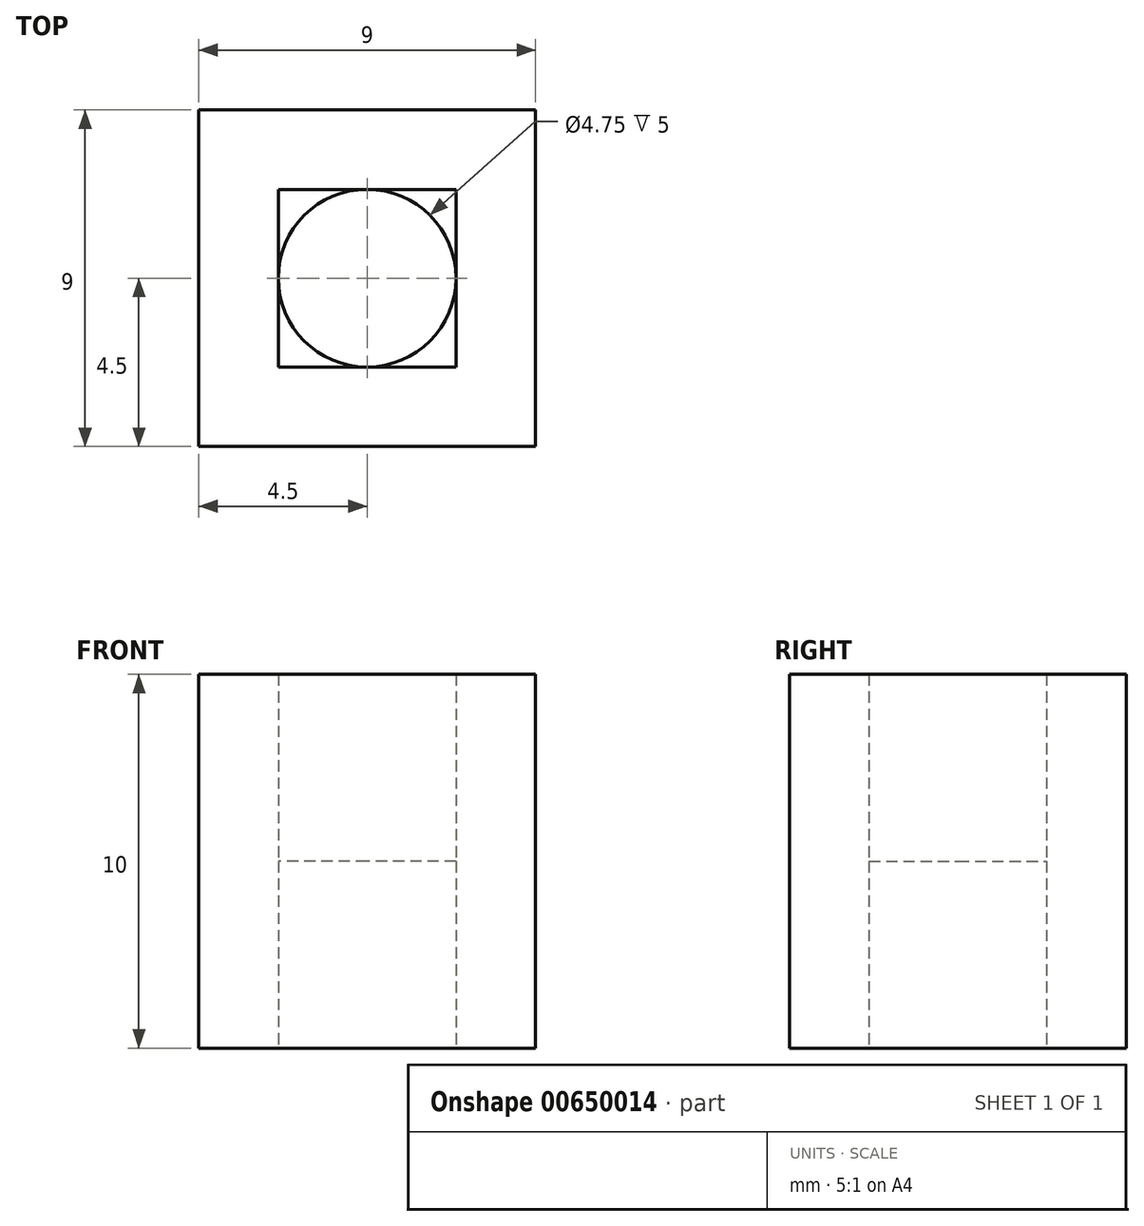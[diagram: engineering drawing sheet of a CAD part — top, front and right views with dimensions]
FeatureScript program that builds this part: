
annotation { "Feature Type Name" : "Feature", "Feature Type Description" : "" }
export const myFeature = defineFeature(function(context is Context, id is Id, definition is map)
    precondition{}
    {
        {
            var Q0;
            Q0=qCreatedBy(makeId("Top.planeOp"),FACE);
            var sketch = newSketch(context, id + "F0", { "sketchPlane" : qUnion([Q0])});
            skCircle(sketch, "E0", {"center": v(0, 0) * mm, "radius": 4.5 * mm});
            skCircle(sketch, "E1", {"center": v(0, 0) * mm, "radius": 2.38 * mm});
            skLineSegment(sketch, "E2.bottom", {"start": v(4.5, -4.5) * mm, "end": v(-4.5, -4.5) * mm});
            skLineSegment(sketch, "E2.top", {"start": v(4.5, 4.5) * mm, "end": v(-4.5, 4.5) * mm});
            skLineSegment(sketch, "E2.left", {"start": v(4.5, -4.5) * mm, "end": v(4.5, 4.5) * mm});
            skLineSegment(sketch, "E2.right", {"start": v(-4.5, -4.5) * mm, "end": v(-4.5, 4.5) * mm});
            skLineSegment(sketch, "E3.bottom", {"start": v(2.38, -2.38) * mm, "end": v(-2.38, -2.38) * mm});
            skLineSegment(sketch, "E3.top", {"start": v(2.38, 2.38) * mm, "end": v(-2.38, 2.38) * mm});
            skLineSegment(sketch, "E3.left", {"start": v(2.38, -2.38) * mm, "end": v(2.38, 2.38) * mm});
            skLineSegment(sketch, "E3.right", {"start": v(-2.38, -2.38) * mm, "end": v(-2.38, 2.38) * mm});
            skSolve(sketch);
        }
        {
            var Q0;
            Q0=makeQuery(id+"F0.imprint","IMPRINT",FACE,{"disambiguationData":[TD([[makeQuery(id+"F0.imprint","IMPRINT",EDGE,{"derivedFrom":sQuery(id+"F0.wireOp",EDGE,"E0")}),1.0]])]});
            var Q1;
            {var subQ0=sQuery(id+"F0.wireOp",EDGE,"E2.top");var subQ1=sQuery(id+"F0.wireOp",EDGE,"E0");var subQ2=makeQuery(id+"F0.imprint","INTERSECT",VERTEX,{"derivedFrom":[subQ1,subQ0]});Q1=makeQuery(id+"F0.imprint","IMPRINT",FACE,{"disambiguationData":[TD([[makeQuery(id+"F0.imprint","IMPRINT",EDGE,{"disambiguationData":[TD([[subQ2,-1.0]])],"derivedFrom":subQ1}),-1.0]])]});}
            var Q2;
            {var subQ0=sQuery(id+"F0.wireOp",EDGE,"E2.top");var subQ1=sQuery(id+"F0.wireOp",EDGE,"E0");var subQ2=makeQuery(id+"F0.imprint","INTERSECT",VERTEX,{"derivedFrom":[subQ1,subQ0]});Q2=makeQuery(id+"F0.imprint","IMPRINT",FACE,{"disambiguationData":[TD([[makeQuery(id+"F0.imprint","IMPRINT",EDGE,{"disambiguationData":[TD([[subQ2,1.0]])],"derivedFrom":subQ1}),-1.0]])]});}
            var Q3;
            {var subQ0=sQuery(id+"F0.wireOp",EDGE,"E2.left");var subQ1=sQuery(id+"F0.wireOp",EDGE,"E0");var subQ2=makeQuery(id+"F0.imprint","INTERSECT",VERTEX,{"derivedFrom":[subQ1,subQ0]});Q3=makeQuery(id+"F0.imprint","IMPRINT",FACE,{"disambiguationData":[TD([[makeQuery(id+"F0.imprint","IMPRINT",EDGE,{"disambiguationData":[TD([[subQ2,1.0]])],"derivedFrom":subQ1}),-1.0]])]});}
            var Q4;
            {var subQ0=sQuery(id+"F0.wireOp",EDGE,"E2.right");var subQ1=sQuery(id+"F0.wireOp",EDGE,"E0");var subQ2=makeQuery(id+"F0.imprint","INTERSECT",VERTEX,{"derivedFrom":[subQ1,subQ0]});Q4=makeQuery(id+"F0.imprint","IMPRINT",FACE,{"disambiguationData":[TD([[makeQuery(id+"F0.imprint","IMPRINT",EDGE,{"disambiguationData":[TD([[subQ2,-1.0]])],"derivedFrom":subQ1}),-1.0]])]});}
            var Q5;
            {var subQ0=sQuery(id+"F0.wireOp",EDGE,"E3.top");var subQ1=sQuery(id+"F0.wireOp",EDGE,"E1");var subQ2=makeQuery(id+"F0.imprint","INTERSECT",VERTEX,{"derivedFrom":[subQ1,subQ0]});Q5=makeQuery(id+"F0.imprint","IMPRINT",FACE,{"disambiguationData":[TD([[makeQuery(id+"F0.imprint","IMPRINT",EDGE,{"disambiguationData":[TD([[subQ2,-1.0]])],"derivedFrom":subQ1}),-1.0]])]});}
            var Q6;
            {var subQ0=sQuery(id+"F0.wireOp",EDGE,"E3.right");var subQ1=sQuery(id+"F0.wireOp",EDGE,"E1");var subQ2=makeQuery(id+"F0.imprint","INTERSECT",VERTEX,{"derivedFrom":[subQ1,subQ0]});Q6=makeQuery(id+"F0.imprint","IMPRINT",FACE,{"disambiguationData":[TD([[makeQuery(id+"F0.imprint","IMPRINT",EDGE,{"disambiguationData":[TD([[subQ2,-1.0]])],"derivedFrom":subQ1}),-1.0]])]});}
            var Q7;
            {var subQ0=sQuery(id+"F0.wireOp",EDGE,"E3.left");var subQ1=sQuery(id+"F0.wireOp",EDGE,"E1");var subQ2=makeQuery(id+"F0.imprint","INTERSECT",VERTEX,{"derivedFrom":[subQ1,subQ0]});Q7=makeQuery(id+"F0.imprint","IMPRINT",FACE,{"disambiguationData":[TD([[makeQuery(id+"F0.imprint","IMPRINT",EDGE,{"disambiguationData":[TD([[subQ2,1.0]])],"derivedFrom":subQ1}),-1.0]])]});}
            var Q8;
            {var subQ0=sQuery(id+"F0.wireOp",EDGE,"E3.top");var subQ1=sQuery(id+"F0.wireOp",EDGE,"E1");var subQ2=makeQuery(id+"F0.imprint","INTERSECT",VERTEX,{"derivedFrom":[subQ1,subQ0]});Q8=makeQuery(id+"F0.imprint","IMPRINT",FACE,{"disambiguationData":[TD([[makeQuery(id+"F0.imprint","IMPRINT",EDGE,{"disambiguationData":[TD([[subQ2,1.0]])],"derivedFrom":subQ1}),-1.0]])]});}
            extrude(context, id + "F1", {"entities" : qUnion([Q0, Q1, Q2, Q3, Q4, Q5, Q6, Q7, Q8]), "depth" : 5 * mm, "offsetDistance" : 25 * mm});
        }
        {
            var Q0;
            {var subQ0=sQuery(id+"F0.wireOp",EDGE,"E2.top");var subQ1=sQuery(id+"F0.wireOp",EDGE,"E0");var subQ2=makeQuery(id+"F0.imprint","INTERSECT",VERTEX,{"derivedFrom":[subQ1,subQ0]});Q0=makeQuery(id+"F0.imprint","IMPRINT",FACE,{"disambiguationData":[TD([[makeQuery(id+"F0.imprint","IMPRINT",EDGE,{"disambiguationData":[TD([[subQ2,-1.0]])],"derivedFrom":subQ1}),-1.0]])]});}
            var Q1;
            {var subQ12=sQuery(id+"F0.wireOp",EDGE,"E0");var subQ13=makeQuery(id+"F0.imprint","INTERSECT",VERTEX,{"derivedFrom":[subQ12,sQuery(id+"F0.wireOp",EDGE,"E2.top")]});Q1=makeQuery(id+"F0.imprint","IMPRINT",FACE,{"disambiguationData":[TD([[makeQuery(id+"F0.imprint","IMPRINT",EDGE,{"disambiguationData":[TD([[subQ13,1.0]])],"derivedFrom":subQ12}),1.0]])]});}
            var Q2;
            {var subQ0=sQuery(id+"F0.wireOp",EDGE,"E2.right");var subQ1=sQuery(id+"F0.wireOp",EDGE,"E0");var subQ2=makeQuery(id+"F0.imprint","INTERSECT",VERTEX,{"derivedFrom":[subQ1,subQ0]});Q2=makeQuery(id+"F0.imprint","IMPRINT",FACE,{"disambiguationData":[TD([[makeQuery(id+"F0.imprint","IMPRINT",EDGE,{"disambiguationData":[TD([[subQ2,-1.0]])],"derivedFrom":subQ1}),-1.0]])]});}
            var Q3;
            {var subQ0=sQuery(id+"F0.wireOp",EDGE,"E2.left");var subQ1=sQuery(id+"F0.wireOp",EDGE,"E0");var subQ2=makeQuery(id+"F0.imprint","INTERSECT",VERTEX,{"derivedFrom":[subQ1,subQ0]});Q3=makeQuery(id+"F0.imprint","IMPRINT",FACE,{"disambiguationData":[TD([[makeQuery(id+"F0.imprint","IMPRINT",EDGE,{"disambiguationData":[TD([[subQ2,1.0]])],"derivedFrom":subQ1}),-1.0]])]});}
            var Q4;
            {var subQ0=sQuery(id+"F0.wireOp",EDGE,"E2.top");var subQ1=sQuery(id+"F0.wireOp",EDGE,"E0");var subQ2=makeQuery(id+"F0.imprint","INTERSECT",VERTEX,{"derivedFrom":[subQ1,subQ0]});Q4=makeQuery(id+"F0.imprint","IMPRINT",FACE,{"disambiguationData":[TD([[makeQuery(id+"F0.imprint","IMPRINT",EDGE,{"disambiguationData":[TD([[subQ2,1.0]])],"derivedFrom":subQ1}),-1.0]])]});}
            extrude(context, id + "F2", {"entities" : qUnion([Q0, Q1, Q2, Q3, Q4]), "operationType" : NewBodyOperationType.ADD, "depth" : 10 * mm, "offsetDistance" : 25 * mm, "hasSecondDirection" : true, "secondDirectionOppositeDirection" : false, "secondDirectionDepth" : 5 * mm});
        }
    });
